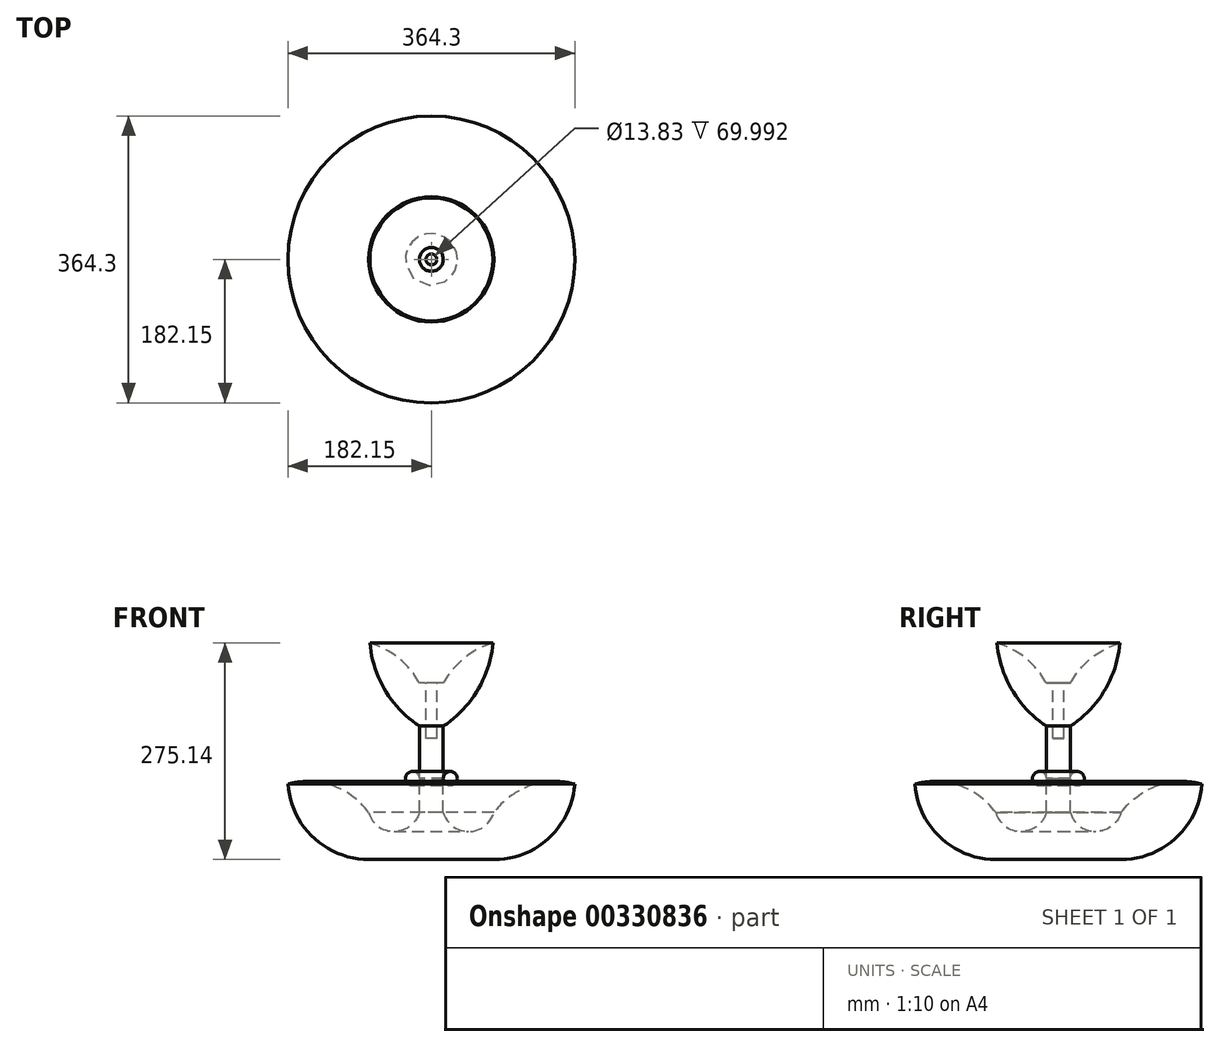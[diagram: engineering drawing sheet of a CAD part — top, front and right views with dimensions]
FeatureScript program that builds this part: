
annotation { "Feature Type Name" : "Feature", "Feature Type Description" : "" }
export const myFeature = defineFeature(function(context is Context, id is Id, definition is map)
    precondition{}
    {
        {
            var Q0;
            Q0=qCreatedBy(makeId("Front.planeOp"),FACE);
            var sketch = newSketch(context, id + "F0", { "sketchPlane" : qUnion([Q0])});
            skLineSegment(sketch, "E0", {"start": v(0, 0) * mm, "end": v(79.6, 0) * mm});
            skArc(sketch, "E1", {"start": v(79.6, 0) * mm, "mid": v(149.76, 27.67) * mm, "end": v(182.15, 95.78) * mm});
            skArc(sketch, "E2", {"start": v(182.15, 95.78) * mm, "mid": v(125.25, 93.55) * mm, "end": v(79.6, 59.53) * mm});
            skArc(sketch, "E3", {"start": v(15.06, 59.9) * mm, "mid": v(47.2, 35.55) * mm, "end": v(79.6, 59.53) * mm});
            skLineSegment(sketch, "E4", {"start": v(15.06, 59.9) * mm, "end": v(15.06, 102.48) * mm});
            skArc(sketch, "E5", {"start": v(15.06, 169.37) * mm, "mid": v(58.77, 214.99) * mm, "end": v(78.1, 275.14) * mm});
            skArc(sketch, "E6", {"start": v(78.1, 275.14) * mm, "mid": v(41.67, 255.61) * mm, "end": v(15.06, 223.99) * mm});
            skLineSegment(sketch, "E7", {"start": v(15.06, 223.99) * mm, "end": v(6.92, 223.99) * mm});
            skLineSegment(sketch, "E8", {"start": v(6.92, 223.99) * mm, "end": v(6.92, 154) * mm});
            skLineSegment(sketch, "E9", {"start": v(6.92, 154) * mm, "end": v(0, 154) * mm});
            skLineSegment(sketch, "E10", {"start": v(0, 154) * mm, "end": v(0, 74.3) * mm});
            skLineSegment(sketch, "E11", {"start": v(0, 74.3) * mm, "end": v(0, 0) * mm});
            skArc(sketch, "E12", {"start": v(15.06, 102.48) * mm, "mid": v(32.95, 102.8) * mm, "end": v(15.06, 103.1) * mm});
            skLineSegment(sketch, "E13.trimOffspring", {"start": v(15.06, 103.1) * mm, "end": v(15.06, 169.37) * mm});
            skSolve(sketch);
        }
        {
            var Q0;
            Q0=makeQuery(id+"F0.imprint","IMPRINT",FACE,{"disambiguationData":[TD([[makeQuery(id+"F0.imprint","IMPRINT",EDGE,{"derivedFrom":sQuery(id+"F0.wireOp",EDGE,"E0")}),1.0]])]});
            var Q1;
            Q1=sQuery(id+"F0.wireOp",EDGE,"E11");
            revolve(context, id + "F1", {"entities" : qUnion([Q0]), "axis" : qUnion([Q1]), "revolveType" : RevolveType.FULL});
        }
    });
